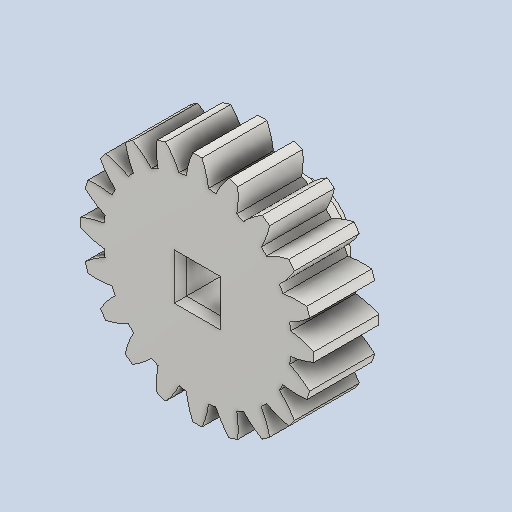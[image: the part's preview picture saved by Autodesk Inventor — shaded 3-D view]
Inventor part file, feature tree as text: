
AUTODESK INVENTOR PART (.ipt)
format: ipt  version: 2022 (Build 260153000, 153)  size: 294,912 bytes
history: native  units: in
note: dims shown in document units (in); Inventor stores cm internally (conversion verified against a paired STEP export)
features: other x12, sketch x4, plane x3
ambient origin geometry x8: Origin, YZ Plane, XZ Plane, XY Plane, X Axis, Y Axis, Z Axis, Center Point
bodies: Solid1 (feature_tree)
feature tree (19):
  other  "Spur Gear24_MIR.ipt"
  other  "Solid1::Spur Gear24_MIR.ipt"
  other  "TaggingFeature1"
  sketch  "Sketch1"  dims[d0=0.3937in]
  sketch  "Sketch2"  dims[d9=0.0in d14=0.0in d15=1.0in d16=0.0in d17=0.0in d18=0.0in d19=1.0in]
  sketch  "Sketch3"
  sketch  "Sketch4"
  plane  "XZ Plane_1"
  plane  "Work Plane2"
  plane  "Work Plane3"
  other  "Srf1"
  other  "Srf1::Derived"
  other  "Start plane iMate"
  other  "Distance iMate"
  other  "Position iMate"
  other  "Mesh iMate"
  other  "Axis iMate"
  other  "Mesh iMate2"
  other  "Align iMate"
